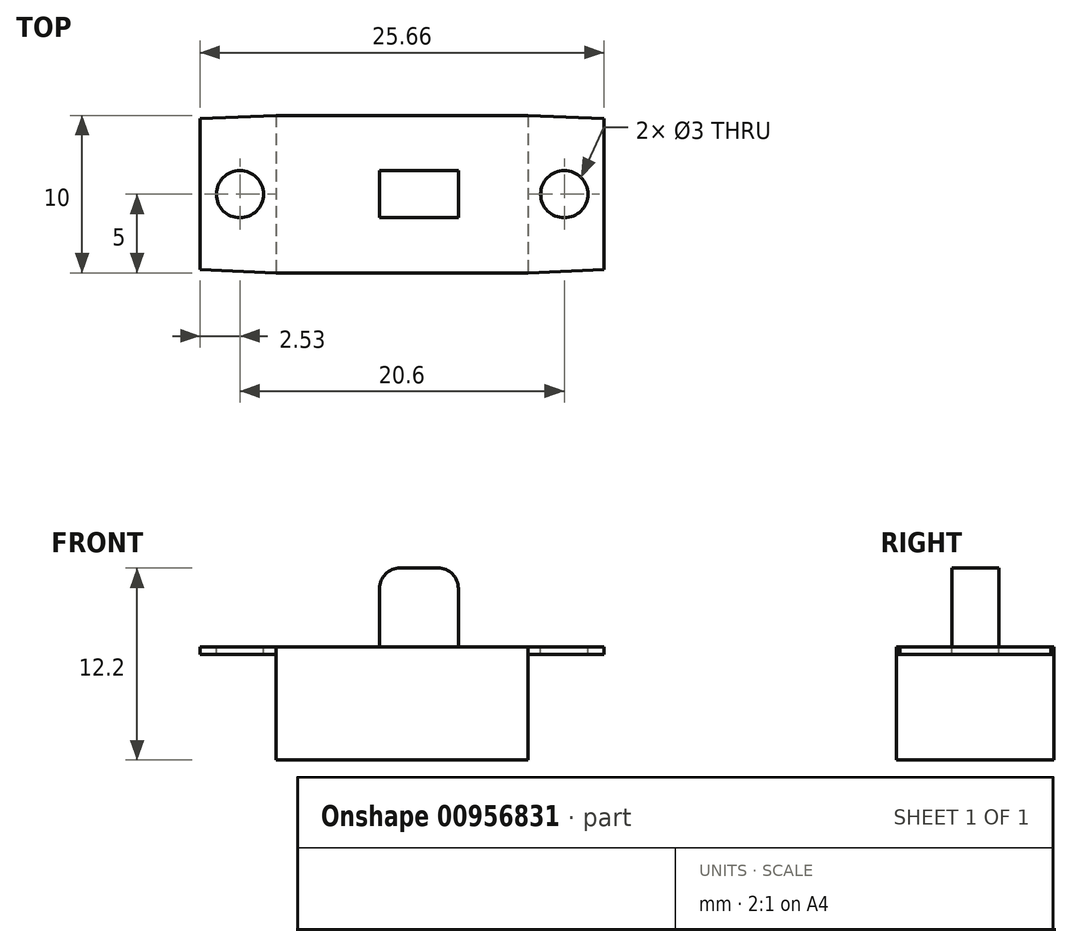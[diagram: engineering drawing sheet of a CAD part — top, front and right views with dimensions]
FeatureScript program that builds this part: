
annotation { "Feature Type Name" : "Feature", "Feature Type Description" : "" }
export const myFeature = defineFeature(function(context is Context, id is Id, definition is map)
    precondition{}
    {
        {
            var Q0;
            Q0=qCreatedBy(makeId("Top.planeOp"),FACE);
            var sketch = newSketch(context, id + "F0", { "sketchPlane" : qUnion([Q0])});
            skLineSegment(sketch, "E0.bottom", {"start": v(8, 5) * mm, "end": v(-8, 5) * mm});
            skLineSegment(sketch, "E0.top", {"start": v(8, -5) * mm, "end": v(-8, -5) * mm});
            skLineSegment(sketch, "E0.left", {"start": v(8, 5) * mm, "end": v(8, -5) * mm});
            skLineSegment(sketch, "E0.right", {"start": v(-8, 5) * mm, "end": v(-8, -5) * mm});
            skPoint(sketch, "E0.middle", {"position": v(0, 0) * mm});
            skSolve(sketch);
        }
        {
            var Q0;
            Q0=qSketchRegion(id+"F0",true);
            extrude(context, id + "F1", {"entities" : qUnion([Q0]), "depth" : 7.2 * mm, "offsetDistance" : 25 * mm});
        }
        {
            var Q0;
            Q0=makeQuery(id+"F1.opExtrude","CAP_FACE",FACE,{"disambiguationData":[OSD([sQuery(id+"F0.wireOp",EDGE,"E0.bottom"),sQuery(id+"F0.wireOp",EDGE,"E0.top"),sQuery(id+"F0.wireOp",EDGE,"E0.left"),sQuery(id+"F0.wireOp",EDGE,"E0.right")])],"isStart":false});
            var sketch = newSketch(context, id + "F2", { "sketchPlane" : qUnion([Q0])});
            skLineSegment(sketch, "E1.bottom", {"start": v(3.57, 1.5) * mm, "end": v(-1.43, 1.5) * mm});
            skLineSegment(sketch, "E1.top", {"start": v(3.57, -1.5) * mm, "end": v(-1.43, -1.5) * mm});
            skLineSegment(sketch, "E1.left", {"start": v(3.57, 1.5) * mm, "end": v(3.57, -1.5) * mm});
            skLineSegment(sketch, "E1.right", {"start": v(-1.43, 1.5) * mm, "end": v(-1.43, -1.5) * mm});
            skPoint(sketch, "E1.middle", {"position": v(1.07, 0) * mm});
            skSolve(sketch);
        }
        {
            var Q0;
            Q0=qSketchRegion(id+"F2",true);
            extrude(context, id + "F3", {"entities" : qUnion([Q0]), "operationType" : NewBodyOperationType.ADD, "depth" : 5 * mm, "offsetDistance" : 25 * mm});
        }
        {
            var Q0;
            Q0=makeQuery(id+"F3.opExtrude","CAP_EDGE",EDGE,{"disambiguationData":[OSD([sQuery(id+"F2.wireOp",EDGE,"E1.right")])],"isStart":false});
            var Q1;
            Q1=makeQuery(id+"F3.opExtrude","CAP_EDGE",EDGE,{"disambiguationData":[OSD([sQuery(id+"F2.wireOp",EDGE,"E1.left")])],"isStart":false});
            fillet(context, id + "F4", {"entities" : qUnion([Q0, Q1]), "radius" : 1.3 * mm, "tangentPropagation" : true, "allowEdgeOverflow" : false});
        }
        {
            var Q0;
            Q0=makeQuery(id+"F1.opExtrude","CAP_FACE",FACE,{"disambiguationData":[OSD([sQuery(id+"F0.wireOp",EDGE,"E0.bottom"),sQuery(id+"F0.wireOp",EDGE,"E0.top"),sQuery(id+"F0.wireOp",EDGE,"E0.left"),sQuery(id+"F0.wireOp",EDGE,"E0.right")])],"isStart":false});
            var sketch = newSketch(context, id + "F5", { "sketchPlane" : qUnion([Q0])});
            skLineSegment(sketch, "E2", {"start": v(-8, 5) * mm, "end": v(0, 5) * mm});
            skLineSegment(sketch, "E3", {"start": v(-8, 5) * mm, "end": v(-12.83, 4.8) * mm});
            skLineSegment(sketch, "E4", {"start": v(-12.83, 4.8) * mm, "end": v(-12.83, 0) * mm});
            skLineSegment(sketch, "E5", {"start": v(0, 0) * mm, "end": v(-31.16, 0) * mm, "construction": true});
            skLineSegment(sketch, "E6", {"start": v(0, 0) * mm, "end": v(0, -18.65) * mm, "construction": true});
            skPoint(sketch, "E6.endSnap0", {"position": v(0, -5) * mm});
            skLineSegment(sketch, "E7.MirrorCS", {"start": v(8, 5) * mm, "end": v(0, 5) * mm});
            skLineSegment(sketch, "E8.MirrorCS", {"start": v(12.83, 4.8) * mm, "end": v(12.83, 0) * mm});
            skLineSegment(sketch, "E9.MirrorCS", {"start": v(8, 5) * mm, "end": v(12.83, 4.8) * mm});
            skLineSegment(sketch, "E10.MirrorCS", {"start": v(12.83, -4.8) * mm, "end": v(12.83, 0) * mm});
            skLineSegment(sketch, "E11.MirrorCS", {"start": v(-12.83, -4.8) * mm, "end": v(-12.83, 0) * mm});
            skLineSegment(sketch, "E12.MirrorCS", {"start": v(-8, -5) * mm, "end": v(-12.83, -4.8) * mm});
            skLineSegment(sketch, "E13.MirrorCS", {"start": v(8, -5) * mm, "end": v(12.83, -4.8) * mm});
            skLineSegment(sketch, "E14.MirrorCS", {"start": v(8, -5) * mm, "end": v(0, -5) * mm});
            skLineSegment(sketch, "E15.MirrorCS", {"start": v(-8, -5) * mm, "end": v(0, -5) * mm});
            skCircle(sketch, "E16", {"center": v(-10.3, 0) * mm, "radius": 1.5 * mm});
            skCircle(sketch, "E17.MirrorC", {"center": v(10.3, 0) * mm, "radius": 1.5 * mm});
            skSolve(sketch);
        }
        {
            var Q0;
            Q0=qSketchRegion(id+"F5",true);
            extrude(context, id + "F6", {"entities" : qUnion([Q0]), "operationType" : NewBodyOperationType.ADD, "oppositeDirection" : true, "depth" : .5 * mm, "offsetDistance" : 25 * mm});
        }
    });
